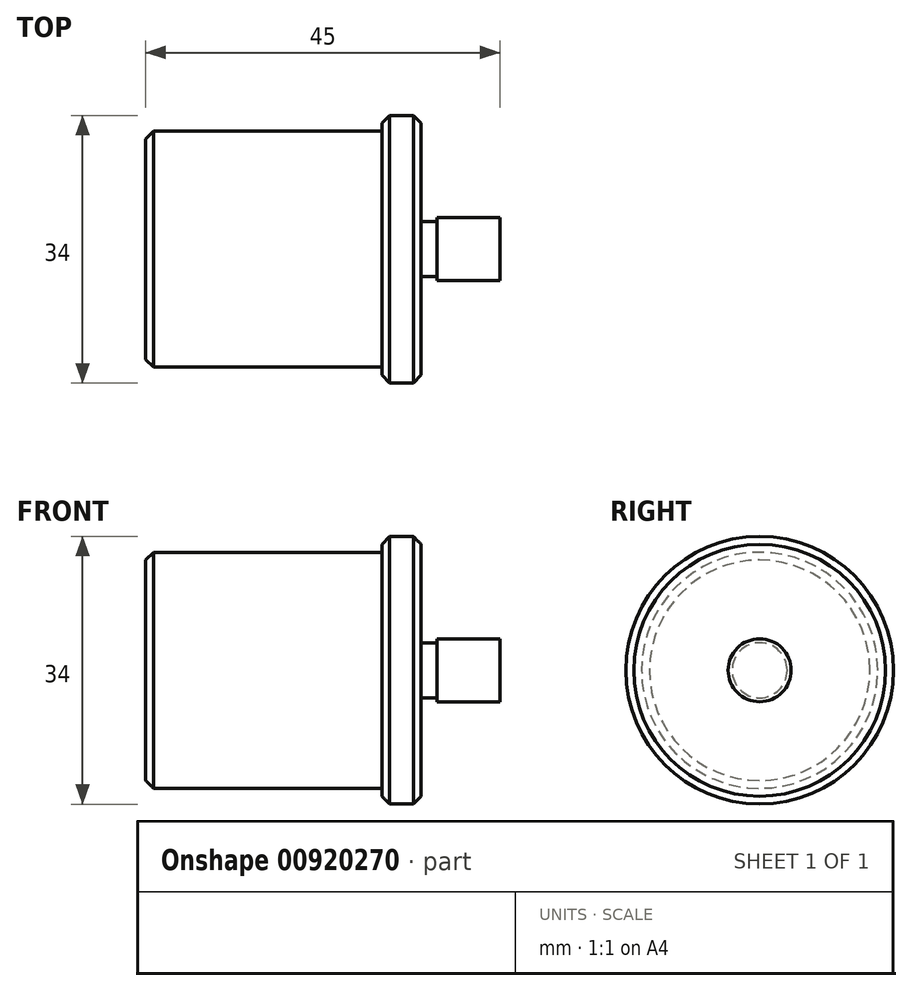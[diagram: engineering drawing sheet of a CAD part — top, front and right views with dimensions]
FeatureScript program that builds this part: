
annotation { "Feature Type Name" : "Feature", "Feature Type Description" : "" }
export const myFeature = defineFeature(function(context is Context, id is Id, definition is map)
    precondition{}
    {
        {
            var Q0;
            Q0=qCreatedBy(makeId("Front.planeOp"),FACE);
            var sketch = newSketch(context, id + "F0", { "sketchPlane" : qUnion([Q0])});
            skLineSegment(sketch, "E0", {"start": v(-72.4, 19.5) * mm, "end": v(-42.4, 19.5) * mm});
            skLineSegment(sketch, "E1", {"start": v(-42.4, 19.5) * mm, "end": v(-42.4, 17.5) * mm});
            skLineSegment(sketch, "E2", {"start": v(-42.4, 17.5) * mm, "end": v(-37.4, 17.5) * mm});
            skLineSegment(sketch, "E3", {"start": v(-37.4, 17.5) * mm, "end": v(-37.4, 30.5) * mm});
            skLineSegment(sketch, "E4", {"start": v(-35.4, 30.5) * mm, "end": v(-27.4, 30.5) * mm});
            skLineSegment(sketch, "E5", {"start": v(-27.4, 30.5) * mm, "end": v(-27.4, 34.5) * mm});
            skLineSegment(sketch, "E6", {"start": v(-27.4, 34.5) * mm, "end": v(-72.4, 34.5) * mm});
            skLineSegment(sketch, "E7", {"start": v(-72.4, 34.5) * mm, "end": v(-72.4, 19.5) * mm});
            skLineSegment(sketch, "E8.top", {"start": v(-37.4, 31) * mm, "end": v(-35.4, 31) * mm});
            skLineSegment(sketch, "E8.left", {"start": v(-37.4, 30.5) * mm, "end": v(-37.4, 31) * mm});
            skLineSegment(sketch, "E8.right", {"start": v(-35.4, 30.5) * mm, "end": v(-35.4, 31) * mm});
            skSolve(sketch);
        }
        {
            var Q0;
            Q0=makeQuery(id+"F0.imprint","IMPRINT",FACE,{"disambiguationData":[TD([[makeQuery(id+"F0.imprint","IMPRINT",EDGE,{"derivedFrom":sQuery(id+"F0.wireOp",EDGE,"E0")}),1.0]])]});
            var Q1;
            Q1=sQuery(id+"F0.wireOp",EDGE,"E6");
            revolve(context, id + "F1", {"entities" : qUnion([Q0]), "axis" : qUnion([Q1]), "revolveType" : RevolveType.FULL});
        }
        {
            var Q0;
            Q0=makeQuery(id+"F1.opRevolve","SWEPT_EDGE",EDGE,{"disambiguationData":[OSD([sQuery(id+"F0.wireOp",EDGE,"E2"),sQuery(id+"F0.wireOp",EDGE,"E3")])]});
            var Q1;
            Q1=makeQuery(id+"F1.opRevolve","SWEPT_EDGE",EDGE,{"disambiguationData":[OSD([sQuery(id+"F0.wireOp",EDGE,"E1"),sQuery(id+"F0.wireOp",EDGE,"E2")])]});
            var Q2;
            Q2=makeQuery(id+"F1.opRevolve","SWEPT_EDGE",EDGE,{"disambiguationData":[OSD([sQuery(id+"F0.wireOp",EDGE,"E0"),sQuery(id+"F0.wireOp",EDGE,"E7")])]});
            chamfer(context, id + "F2", {"entities" : qUnion([Q0, Q1, Q2]), "width" : 1 * mm, "tangentPropagation" : true});
        }
    });
